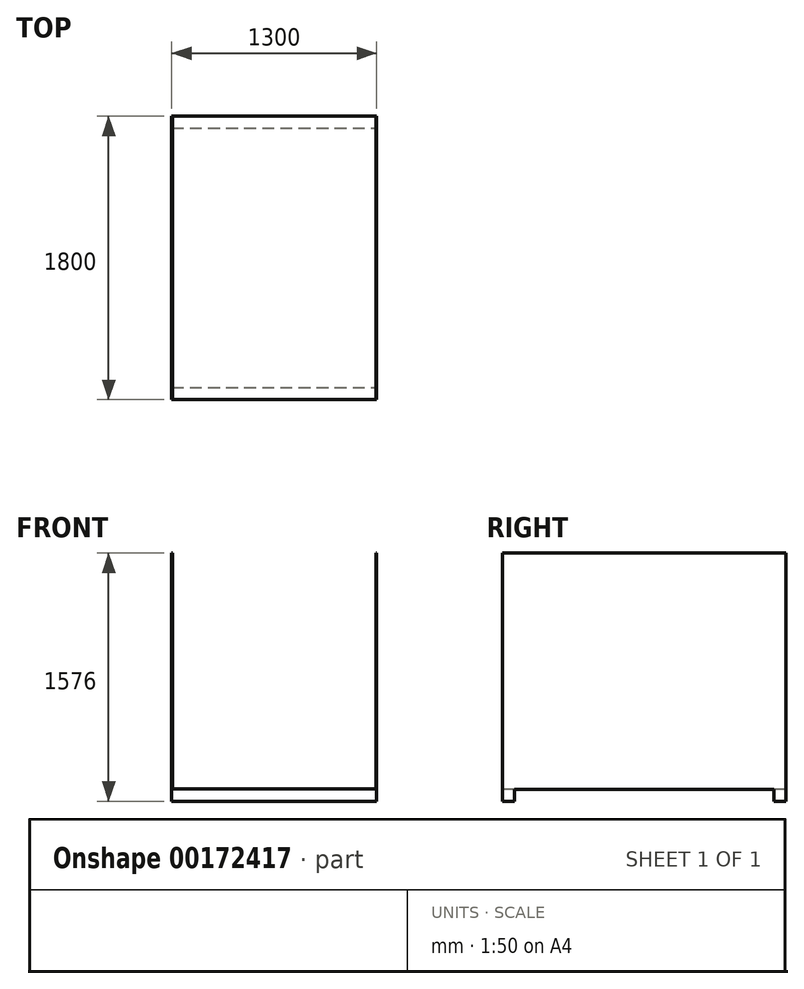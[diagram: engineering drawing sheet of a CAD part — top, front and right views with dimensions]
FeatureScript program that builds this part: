
annotation { "Feature Type Name" : "Feature", "Feature Type Description" : "" }
export const myFeature = defineFeature(function(context is Context, id is Id, definition is map)
    precondition{}
    {
        {
            var Q0;
            Q0=qCreatedBy(makeId("Front.planeOp"),FACE);
            var sketch = newSketch(context, id + "F0", { "sketchPlane" : qUnion([Q0])});
            skLineSegment(sketch, "E0", {"start": v(2.17, 1446.44) * mm, "end": v(2.17, -49.56) * mm});
            skLineSegment(sketch, "E1", {"start": v(2.17, -49.56) * mm, "end": v(1294.17, -49.56) * mm});
            skLineSegment(sketch, "E2", {"start": v(1294.17, -49.56) * mm, "end": v(1294.17, 1446.44) * mm});
            skLineSegment(sketch, "E3", {"start": v(1294.17, 1446.44) * mm, "end": v(1298.17, 1446.44) * mm});
            skLineSegment(sketch, "E4", {"start": v(1298.17, 1446.44) * mm, "end": v(1298.17, -53.56) * mm});
            skLineSegment(sketch, "E5", {"start": v(1298.17, -53.56) * mm, "end": v(-1.83, -53.56) * mm});
            skLineSegment(sketch, "E6", {"start": v(-1.83, -53.56) * mm, "end": v(-1.83, 1446.44) * mm});
            skLineSegment(sketch, "E7", {"start": v(-1.83, 1446.44) * mm, "end": v(2.17, 1446.44) * mm});
            skSolve(sketch);
        }
        {
            var Q0;
            Q0=makeQuery(id+"F0.imprint","IMPRINT",FACE,{"disambiguationData":[TD([[makeQuery(id+"F0.imprint","IMPRINT",EDGE,{"derivedFrom":sQuery(id+"F0.wireOp",EDGE,"E0")}),-1.0]])]});
            extrude(context, id + "F1", {"entities" : qUnion([Q0]), "depth" : 1800 * mm});
        }
        {
            var Q0;
            Q0=makeQuery(id+"F1.opExtrude","SWEPT_FACE",FACE,{"disambiguationData":[OSD([sQuery(id+"F0.wireOp",EDGE,"E4")])]});
            var sketch = newSketch(context, id + "F2", { "sketchPlane" : qUnion([Q0])});
            skLineSegment(sketch, "E8.bottom", {"start": v(-1800, -53.56) * mm, "end": v(-1724, -53.56) * mm});
            skLineSegment(sketch, "E8.top", {"start": v(-1800, -129.56) * mm, "end": v(-1724, -129.56) * mm});
            skLineSegment(sketch, "E8.left", {"start": v(-1800, -53.56) * mm, "end": v(-1800, -129.56) * mm});
            skLineSegment(sketch, "E8.right", {"start": v(-1724, -53.56) * mm, "end": v(-1724, -129.56) * mm});
            skLineSegment(sketch, "E9.bottom", {"start": v(0, -53.56) * mm, "end": v(-76, -53.56) * mm});
            skLineSegment(sketch, "E9.top", {"start": v(0, -129.56) * mm, "end": v(-76, -129.56) * mm});
            skLineSegment(sketch, "E9.left", {"start": v(0, -53.56) * mm, "end": v(0, -129.56) * mm});
            skLineSegment(sketch, "E9.right", {"start": v(-76, -53.56) * mm, "end": v(-76, -129.56) * mm});
            skSolve(sketch);
        }
        {
            var Q0;
            Q0=makeQuery(id+"F2.imprint","IMPRINT",FACE,{"disambiguationData":[TD([[makeQuery(id+"F2.imprint","IMPRINT",EDGE,{"derivedFrom":sQuery(id+"F2.wireOp",EDGE,"E9.bottom")}),-1.0]])]});
            var Q1;
            Q1=makeQuery(id+"F2.imprint","IMPRINT",FACE,{"disambiguationData":[TD([[makeQuery(id+"F2.imprint","IMPRINT",EDGE,{"derivedFrom":sQuery(id+"F2.wireOp",EDGE,"E8.bottom")}),-1.0]])]});
            extrude(context, id + "F3", {"entities" : qUnion([Q0, Q1]), "operationType" : NewBodyOperationType.ADD, "oppositeDirection" : true, "depth" : 1300 * mm});
        }
    });
